FCSTD DOCUMENT  (FreeCAD 1.1R20260414 (Git shallow))
Label: V
Comment: Source: ServoQuetsch https://gitlab.com/mikeventor1/ServoQuetsch (CERN-OHL-P-2.0). Multi-file bundle: parts driven by VarSet in V.FCStd.
License: CERN Open Hardware Licence Version 2 - Permissive
LicenseURL: https://ohwr.org/cernohl
objects: Sketcher::SketchObject×5, App::Point×1, App::VarSet×1, PartDesign::Body×1
note: 11 computed .brp shape members not serialized (recipe doc carries the construction recipe); baked Part::Feature solids carry a one-line shape summary decoded from their .brp

FEATURE [Sketcher::SketchObject] Sketch  label="Tube"
  ArcFitTolerance = 1e-06
  AttachmentSupport = -> [XZ_Plane]
  ExternalTypes = [0]
  FullyConstrained = true
  MakeInternals = false
  MapMode = 5
  Placement = pos=(0,0,0) rot=(1,0,0;1.5708rad)
  _ExternalGeoVersion = 1
  sketch-geometry (2):
    g0: Circle CenterX=0 CenterY=0 CenterZ=0 NormalX=0 NormalY=0 NormalZ=1 AngleXU=0 Radius=1.5
    g1: Circle CenterX=0 CenterY=0 CenterZ=0 NormalX=0 NormalY=0 NormalZ=1 AngleXU=0 Radius=0.75
  constraints (4):
    c: Coincident(g0,g-1)
    c: Coincident(g1,g0)
    c: Diameter(g1) = 1.5  'TubeID'
    c: Diameter(g0) = 3  'TubeOD'
FEATURE [App::Point] Origin001  label="Ursprung"
  Role = Origin
FEATURE [Sketcher::SketchObject] Sketch001  label="ValveTop"
  ArcFitTolerance = 1e-06
  AttachmentSupport = -> [Origin]
  ExternalGeometry = -> [Sketch]
  ExternalTypes = [0,0]
  FullyConstrained = true
  MakeInternals = false
  MapMode = 5
  _ExternalGeoVersion = 1
  sketch-geometry (5):
    g0: LineSegment StartX=-4.5 StartY=27.5 StartZ=0 EndX=-4.5 EndY=-27.5 EndZ=0
    g1: LineSegment StartX=-4.5 StartY=-27.5 StartZ=0 EndX=28 EndY=-27.5 EndZ=0
    g2: LineSegment StartX=28 StartY=-27.5 StartZ=0 EndX=28 EndY=27.5 EndZ=0
    g3: LineSegment StartX=28 StartY=27.5 StartZ=0 EndX=-4.5 EndY=27.5 EndZ=0
    g4: LineSegment [constr] StartX=-1.5 StartY=0 StartZ=0 EndX=-4.5 EndY=0 EndZ=0
  constraints (13):
    c: Coincident(g0,g1)
    c: Coincident(g1,g2)
    c: Coincident(g2,g3)
    c: Coincident(g3,g0)
    c: Vertical(g2)
    c: Horizontal(g1)
    c: Horizontal(g3)
    c: Symmetric(g0,g0,g-1)
    c: DistanceX(g3,g3) = 32.5  'ValveW'
    c: Coincident(g4,g-3)
    c: Symmetric(g0,g0,g4)
    c: DistanceX(g4,g4) = 3  'WallW'
    c: DistanceY(g2,g2) = 55  'ServoH'
FEATURE [Sketcher::SketchObject] Sketch002  label="Servo"
  ArcFitTolerance = 1e-06
  AttachmentSupport = -> [Origin]
  ExternalGeometry = -> [Sketch001]
  ExternalTypes = [0]
  FullyConstrained = true
  MakeInternals = false
  MapMode = 5
  _ExternalGeoVersion = 1
  sketch-geometry (6):
    g0: LineSegment StartX=1.75 StartY=27.5 StartZ=0 EndX=1.75 EndY=-27.5 EndZ=0
    g1: LineSegment StartX=1.75 StartY=-27.5 StartZ=0 EndX=21.75 EndY=-27.5 EndZ=0
    g2: LineSegment StartX=21.75 StartY=-27.5 StartZ=0 EndX=21.75 EndY=27.5 EndZ=0
    g3: LineSegment StartX=21.75 StartY=27.5 StartZ=0 EndX=1.75 EndY=27.5 EndZ=0
    g4: GeomPoint X=11.75 Y=-1e-16 Z=0
    g5: GeomPoint X=11.75 Y=27.5 Z=0
  constraints (13):
    c: Coincident(g0,g1)
    c: Coincident(g1,g2)
    c: Coincident(g2,g3)
    c: Coincident(g3,g0)
    c: Vertical(g2)
    c: Horizontal(g1)
    c: Horizontal(g3)
    c: Symmetric(g0,g0,g-1)
    c: DistanceX(g3,g3) = 20  'ServoW'
    c: Symmetric(g0,g1,g4)
    c: Symmetric(g-3,g-3,g5)
    c: Vertical(g5,g4)
    c: Horizontal(g-3,g2)
FEATURE [Sketcher::SketchObject] Sketch003  label="ValveSide"
  ArcFitTolerance = 1e-06
  AttachmentSupport = -> [Origin]
  ExternalGeometry = -> [Sketch001]
  ExternalTypes = [0]
  FullyConstrained = true
  MakeInternals = false
  MapMode = 5
  Placement = pos=(0,0,0) rot=(1,0,0;1.5708rad)
  _ExternalGeoVersion = 1
  sketch-geometry (4):
    g0: LineSegment StartX=-4.5 StartY=9 StartZ=0 EndX=-4.5 EndY=-9 EndZ=0
    g1: LineSegment StartX=-4.5 StartY=-9 StartZ=0 EndX=28 EndY=-9 EndZ=0
    g2: LineSegment StartX=28 StartY=-9 StartZ=0 EndX=28 EndY=9 EndZ=0
    g3: LineSegment StartX=28 StartY=9 StartZ=0 EndX=-4.5 EndY=9 EndZ=0
  constraints (11):
    c: Coincident(g0,g1)
    c: Coincident(g1,g2)
    c: Coincident(g2,g3)
    c: Vertical(g0)
    c: Vertical(g2)
    c: Horizontal(g1)
    c: Vertical(g1,g-3)
    c: DistanceY(g2,g2) = 18  'ValveD'
    c: Coincident(g0,g3)
    c: Horizontal(g3)
    c: Symmetric(g0,g0,g-3)
FEATURE [App::VarSet] VarSet
  CutoutH = 15
  PinchBottomT = 1.5
  PinchEndL = 13.25
  PinchStartAngle = 30
  PinchStartL = 10.25
  PinchedTubeW = 0
  PincherH = 8
  ServoClearance = 0.5
  ServoConnectOffset = 0.125
  ServoH = 55
  ServoInnerH = 40
  ServoW = 20
  SevoHeadH = 5
  TubeClearance = 1
  TubeCutW = 0.5
  TubeEndLen = 50
  TubeID = 1.5
  TubeOD = 3
  TubeToWall = 2
  TubeZDist = 11.7
  TubholderT = 2
  ValveD = 18
  ValveHOffset = 20
  ValveW = 32.5
  WallW = 3
  expr: PinchEndL = Sketch004.Constraints.PinchEndL
  expr: PinchStartAngle = Sketch004.Constraints.PinchStartAngle
  expr: PinchStartL = Sketch004.Constraints.PinchStartL
  expr: PinchedTubeW = Sketch004.Constraints.PinchedTubeW
  expr: ServoConnectOffset = 0.125
  expr: ServoH = Sketch001.Constraints.ServoH
  expr: ServoW = Sketch002.Constraints.ServoW
  expr: TubeID = Sketch.Constraints.TubeID
  expr: TubeOD = Sketch.Constraints.TubeOD
  expr: ValveD = Sketch003.Constraints.ValveD
  expr: ValveW = Sketch001.Constraints.ValveW
  expr: WallW = Sketch001.Constraints.WallW
FEATURE [Sketcher::SketchObject] Sketch004  label="Pincher"
  ArcFitTolerance = 1e-06
  AttachmentSupport = -> [Origin]
  ExternalGeometry = -> [Sketch,Sketch002]
  ExternalTypes = [0,0]
  FullyConstrained = true
  MakeInternals = false
  MapMode = 5
  _ExternalGeoVersion = 1
  sketch-geometry (5):
    g0: GeomPoint X=11.75 Y=27.5 Z=0
    g1: GeomPoint X=11.75 Y=0 Z=0
    g2: LineSegment StartX=11.75 StartY=0 StartZ=0 EndX=-1.5 EndY=0 EndZ=0
    g3: LineSegment StartX=11.75 StartY=0 StartZ=0 EndX=2.87324 EndY=-5.125 EndZ=0
    g4: LineSegment [constr] StartX=1.5 StartY=0 StartZ=0 EndX=11.75 EndY=0 EndZ=0
  constraints (13):
    c: Symmetric(g-4,g-4,g0)
    c: PointOnObject(g1,g-1)
    c: Vertical(g0,g1)
    c: Coincident(g2,g1)
    c: PointOnObject(g2,g-1)
    c: DistanceX(g-3,g2) = 0  'PinchedTubeW'
    c: DistanceX(g2,g2) = 13.25  'PinchEndL'
    c: Coincident(g3,g1)
    c: Coincident(g4,g-3)
    c: Coincident(g4,g1)
    c: Equal(g4,g3)
    c: Angle(g2,g3) = 0.523599  'PinchStartAngle'
    c: Distance(g3,g3) = 10.25  'PinchStartL'
FEATURE [PartDesign::Body] Body
  AllowCompound = false
  Group = -> [Sketch,Sketch001,Sketch002,Sketch003,Sketch004]
  Origin = -> Origin
